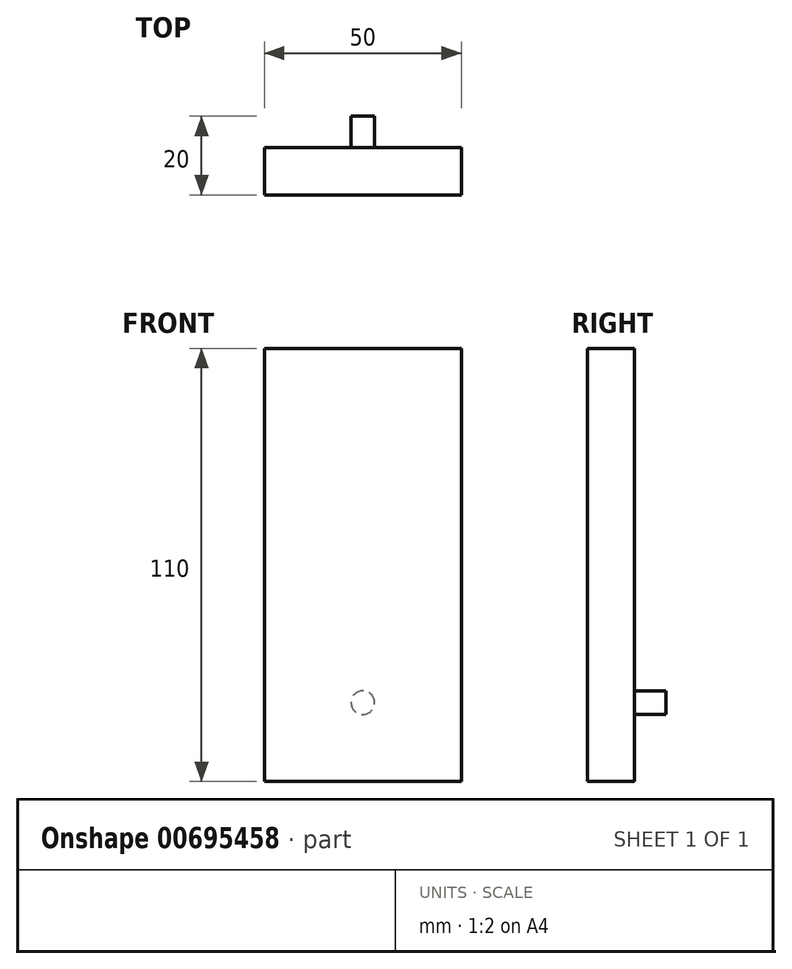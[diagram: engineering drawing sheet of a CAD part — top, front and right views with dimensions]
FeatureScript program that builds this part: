
annotation { "Feature Type Name" : "Feature", "Feature Type Description" : "" }
export const myFeature = defineFeature(function(context is Context, id is Id, definition is map)
    precondition{}
    {
        {
            var Q0;
            Q0=qCreatedBy(makeId("Front.planeOp"),FACE);
            var sketch = newSketch(context, id + "F0", { "sketchPlane" : qUnion([Q0])});
            skLineSegment(sketch, "E0.bottom", {"start": v(-25, 90) * mm, "end": v(25, 90) * mm});
            skLineSegment(sketch, "E0.top", {"start": v(-25, -20) * mm, "end": v(25, -20) * mm});
            skLineSegment(sketch, "E0.left", {"start": v(-25, 90) * mm, "end": v(-25, -20) * mm});
            skLineSegment(sketch, "E0.right", {"start": v(25, 90) * mm, "end": v(25, -20) * mm});
            skSolve(sketch);
        }
        {
            var Q0;
            Q0=makeQuery(id+"F0.imprint","IMPRINT",FACE,{"disambiguationData":[TD([[makeQuery(id+"F0.imprint","IMPRINT",EDGE,{"derivedFrom":sQuery(id+"F0.wireOp",EDGE,"E0.bottom")}),-1.0]])]});
            extrude(context, id + "F1", {"entities" : qUnion([Q0]), "depth" : 20 * mm, "offsetDistance" : 25 * mm});
        }
        {
            var Q0;
            Q0=makeQuery(id+"F1.opExtrude","CAP_FACE",FACE,{"disambiguationData":[OSD([sQuery(id+"F0.wireOp",EDGE,"E0.bottom"),sQuery(id+"F0.wireOp",EDGE,"E0.top"),sQuery(id+"F0.wireOp",EDGE,"E0.left"),sQuery(id+"F0.wireOp",EDGE,"E0.right")])],"isStart":true});
            var sketch = newSketch(context, id + "F2", { "sketchPlane" : qUnion([Q0])});
            skCircle(sketch, "E1", {"center": v(0, 0) * mm, "radius": 3 * mm});
            skSolve(sketch);
        }
        {
            var Q0;
            Q0=makeQuery(id+"F2.imprint","IMPRINT",FACE,{"disambiguationData":[TD([[makeQuery(id+"F2.imprint","IMPRINT",EDGE,{"derivedFrom":sQuery(id+"F2.wireOp",EDGE,"E1")}),-1.0]])]});
            extrude(context, id + "F3", {"entities" : qUnion([Q0]), "operationType" : NewBodyOperationType.REMOVE, "oppositeDirection" : true, "depth" : 8 * mm, "offsetDistance" : 25 * mm});
        }
    });
